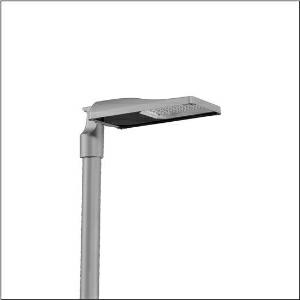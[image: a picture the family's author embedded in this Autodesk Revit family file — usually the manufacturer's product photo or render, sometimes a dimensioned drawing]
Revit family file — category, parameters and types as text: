
# Revit family: streetlight_sl_31_mini___st1_0a_5xh6d31a08ga_ae29
name_source: partatom
category: Lighting Fixtures
units: mm (PartAtom-declared; Revit-internal decimal feet)

## family parameters
Cut with Voids When Loaded = No
Host = Face
Light Source = No
Part Type = Normal
Room Calculation Point = No
Round Connector Dimension = Use Diameter
Shared = No

## types (1)
- --- (1 x LED, 5710 lm, 37.3 W, 3000K)
    Apparent Load = 37 VA
    CIE Flux Codes = 37 72 97 100 100
    Color Rendering = 70
    Color Temperature = 3000K
    Default Elevation = 1800 mm
    Description = Streetlight SL 31 mini Easy, Desk-Remote mast luminaire for post-top, side-entry; light control with lens of PMMA; light distribution: ST1.0a, direct asymmetric distribution, for standard-compliant lighting for roads and squares; LED: luminous flux: 5.710lm, light colour: 730, colour temperature: 3000K; luminous efficacy: 153,1lm/W; control: pre-setting: linear dimming characteristic, flexible luminous flux parameterisation, time-dependent luminous flux control, constant luminous flux control, intelligent temperature release in ECG and LED module, overheat protection; luminaire housing, of diecast aluminium, Siteco® metallic grey (DB 702S), corrosivity category C5 high according to DIN EN ISO 12944; cover of toughened safety glass, transparent, opened without tools; mast flange of diecast aluminium, Siteco® metallic grey (DB 702S), spigot size: 76/60mm, mast flange included unmounted; with cable H07RN-F 2x 1.5mm², cable length: 6,5m, connection cable pre-assembled; mains connection: 220..240V, AC, 50/60Hz; power consumption (at start of service life): 37,3W / (at end of service life): 38,7W / (with reduced operation 50%): 17,5W; protection rating (complete): IP66; insulation class (complete): insulation class II (safety insulation); impact resistance: IK10; certification: CE, ENEC, ENEC+, VDE, UKCA; permissible operating ambient temperature for outdoor applications: -40..+50°C; packaging unit: 1 piece

Light Distribution: ST1.0a
    Height = 76 mm
    Lamp = 1 x LED
    Lamp Light Flux = 5710 lm
    Lamp Power = 37.3 W
    Lamp count = 1
    Length = 547 mm
    Luminous efficacy = 153 lm/W
    Manufacturer = Siteco
    ModVariant = No
    Model = 5XH6D31A08GA
    Number of Poles = 1
    OnlyDefault = Yes
    Power Factor = 1
    Product Name = Streetlight SL 31 mini | ST1.0a
    Product group = mast luminaire | pylon top
    ProductGroupID = 6100
    Protection Class = Protection class II
    Protection Degree = IP 66
    RLX_Detail_Level = 1
    RLX_Emergency_Light_Flux = 0 lm
    RLX_Emergency_Type = 0
    RLX_Emergency_Type_DB = No
    RlxData = <blob elided: 39513 chars, md5=351757b5>
    Socket = socket
    Standby Power = 0 W
    System Light Flux = 5710 lm
    System Power = 37 W
    Type Comments = factory setting: luminous flux: 100 % | dim-lin: 254 | 386 mA
    Type Image = l_1300326.jpg
    URL = http://relux.com
    VarID = @adj_054388
    Voltage = 0 V
    Weight = 0.00 kg
    Width = 265 mm

## geometry (parser evidence)
native form markers: Blend x4, Sweep x8
no freeform markers — native parametric forms only
